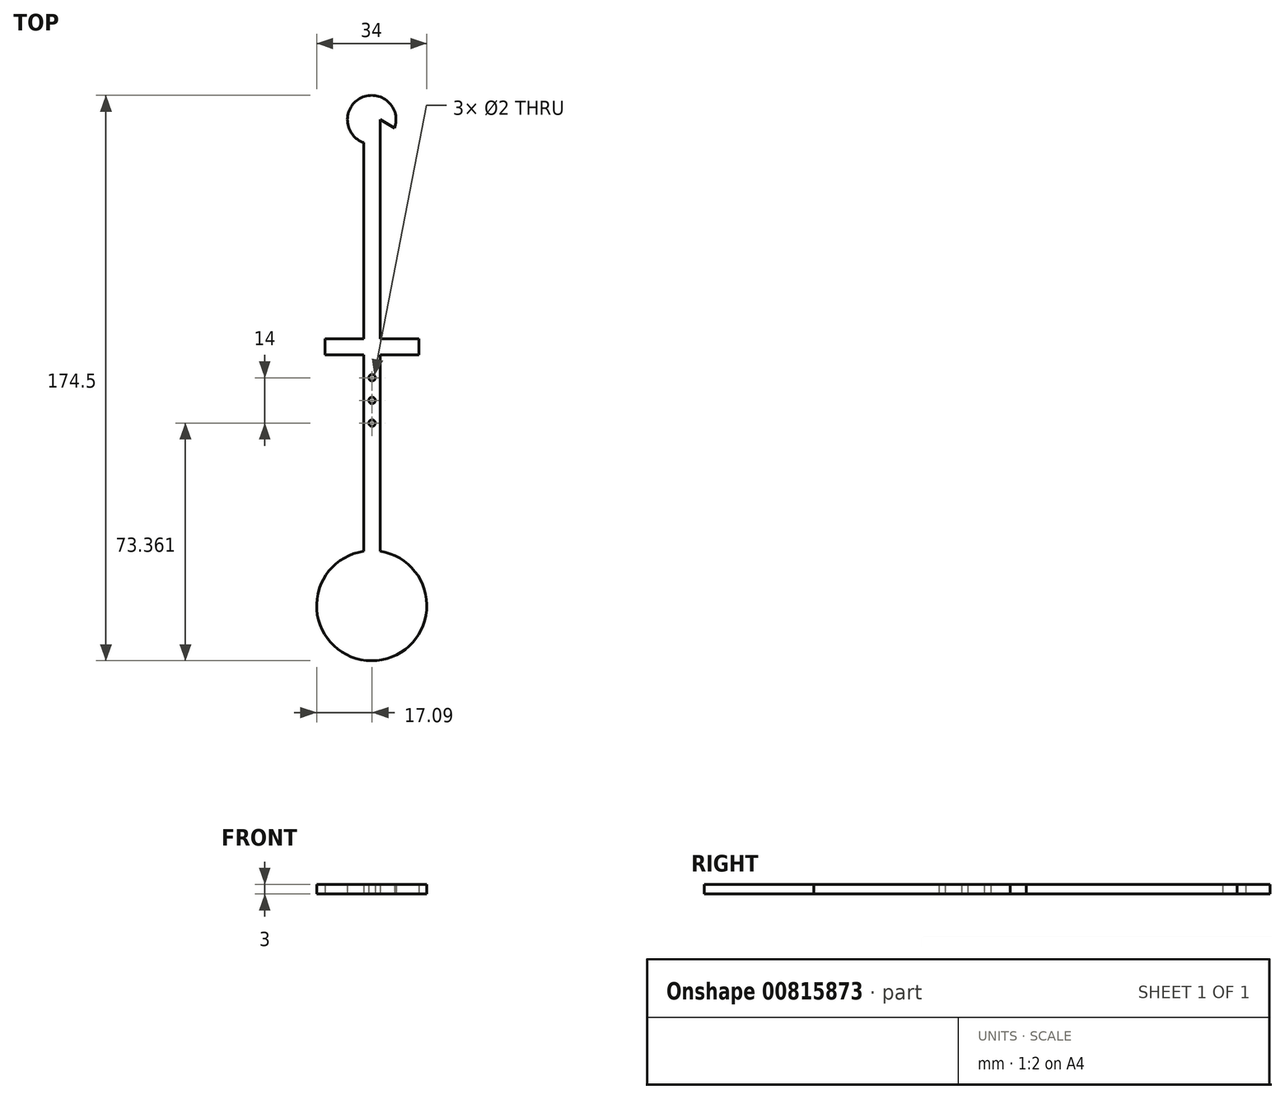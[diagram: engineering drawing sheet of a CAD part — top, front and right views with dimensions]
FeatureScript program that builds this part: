
annotation { "Feature Type Name" : "Feature", "Feature Type Description" : "" }
export const myFeature = defineFeature(function(context is Context, id is Id, definition is map)
    precondition{}
    {
        {
            var Q0;
            Q0=qCreatedBy(makeId("Top.planeOp"),FACE);
            var sketch = newSketch(context, id + "F0", { "sketchPlane" : qUnion([Q0])});
            skArc(sketch, "E0", {"start": v(-3.6, -36.71) * mm, "mid": v(-1.3, -70.54) * mm, "end": v(1.4, -36.74) * mm});
            skArc(sketch, "E1", {"start": v(5.84, 93.87) * mm, "mid": v(-4.44, 103.22) * mm, "end": v(-3.6, 89.36) * mm});
            skLineSegment(sketch, "E2.left", {"start": v(-3.6, 89.36) * mm, "end": v(-3.6, 28.82) * mm});
            skLineSegment(sketch, "E2.right", {"start": v(1.4, 89.42) * mm, "end": v(1.4, 28.82) * mm});
            skLineSegment(sketch, "E3", {"start": v(1.4, 96.46) * mm, "end": v(5.84, 93.87) * mm});
            skLineSegment(sketch, "E4", {"start": v(5.84, 93.87) * mm, "end": v(1.4, 96.46) * mm});
            skLineSegment(sketch, "E5", {"start": v(1.4, 89.42) * mm, "end": v(1.4, 96.46) * mm});
            skPoint(sketch, "E6.orphan", {"position": v(1.4, -53.54) * mm});
            skLineSegment(sketch, "E7.bottom", {"start": v(-15.6, 28.82) * mm, "end": v(-3.6, 28.82) * mm});
            skLineSegment(sketch, "E7.top", {"start": v(-15.6, 23.82) * mm, "end": v(-3.6, 23.82) * mm});
            skLineSegment(sketch, "E7.left", {"start": v(-15.6, 28.82) * mm, "end": v(-15.6, 23.82) * mm});
            skPoint(sketch, "E8", {"position": v(-1.1, 23.82) * mm});
            skPoint(sketch, "E9", {"position": v(1.4, 23.82) * mm});
            skPoint(sketch, "E10", {"position": v(13.4, 12.89) * mm});
            skPoint(sketch, "E11", {"position": v(-3.6, 23.82) * mm});
            skLineSegment(sketch, "E12", {"start": v(1.4, 28.82) * mm, "end": v(13.4, 28.82) * mm});
            skLineSegment(sketch, "E13", {"start": v(13.4, 28.82) * mm, "end": v(13.4, 23.82) * mm});
            skLineSegment(sketch, "E14.trimOffspring", {"start": v(1.4, 23.82) * mm, "end": v(13.4, 23.82) * mm});
            skLineSegment(sketch, "E15.trimOffspring", {"start": v(-3.6, 23.82) * mm, "end": v(-3.6, -36.71) * mm});
            skLineSegment(sketch, "E16.trimOffspring", {"start": v(1.4, 23.82) * mm, "end": v(1.4, -36.74) * mm});
            skCircle(sketch, "E17", {"center": v(-1.1, 16.82) * mm, "radius": 1 * mm});
            skCircle(sketch, "E18", {"center": v(-1.1, 9.82) * mm, "radius": 1 * mm});
            skCircle(sketch, "E19", {"center": v(-1.1, 2.82) * mm, "radius": 1 * mm});
            skSolve(sketch);
        }
        {
            var Q0;
            Q0=makeQuery(id+"F0.imprint","IMPRINT",FACE,{"disambiguationData":[TD([[makeQuery(id+"F0.imprint","IMPRINT",EDGE,{"derivedFrom":sQuery(id+"F0.wireOp",EDGE,"E0")}),1.0]])]});
            extrude(context, id + "F1", {"entities" : qUnion([Q0]), "depth" : 3 * mm, "offsetDistance" : 25 * mm});
        }
    });
